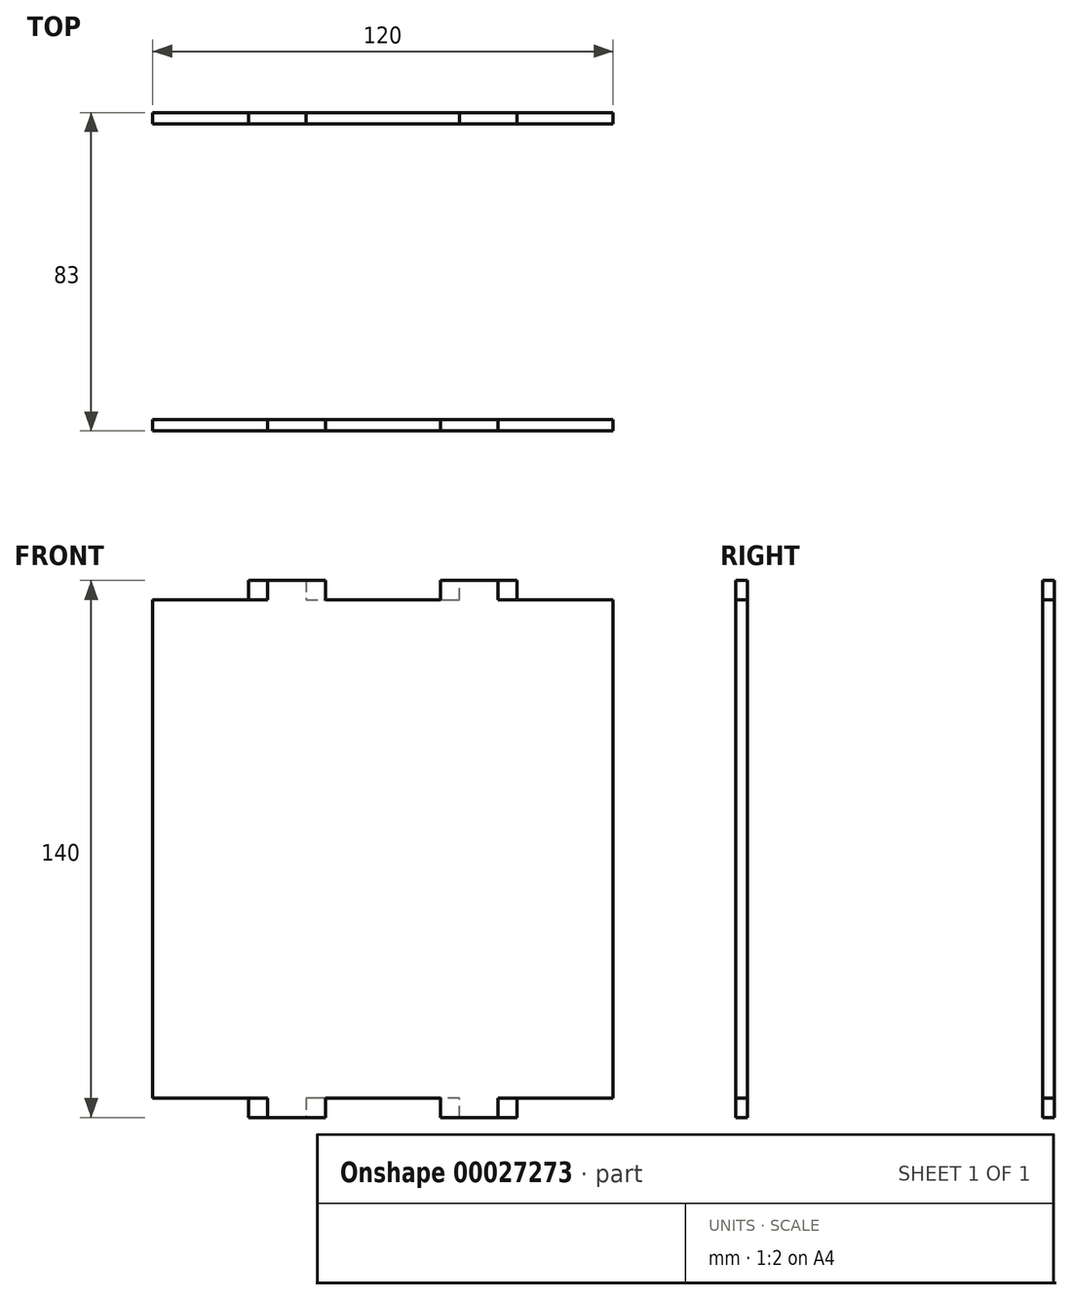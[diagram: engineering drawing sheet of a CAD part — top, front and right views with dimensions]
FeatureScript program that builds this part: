
annotation { "Feature Type Name" : "Feature", "Feature Type Description" : "" }
export const myFeature = defineFeature(function(context is Context, id is Id, definition is map)
    precondition{}
    {
        {
            var Q0;
            Q0=qCreatedBy(makeId("Front.planeOp"),FACE);
            var sketch = newSketch(context, id + "F0", { "sketchPlane" : qUnion([Q0])});
            skLineSegment(sketch, "E0", {"start": v(-60, 65) * mm, "end": v(-35, 65) * mm});
            skLineSegment(sketch, "E1", {"start": v(-35, 65) * mm, "end": v(-35, 70) * mm});
            skLineSegment(sketch, "E2", {"start": v(-35, 70) * mm, "end": v(-20, 70) * mm});
            skLineSegment(sketch, "E3", {"start": v(-20, 70) * mm, "end": v(-20, 65) * mm});
            skLineSegment(sketch, "E4", {"start": v(-20, 65) * mm, "end": v(20, 65) * mm});
            skLineSegment(sketch, "E5", {"start": v(20, 65) * mm, "end": v(20, 70) * mm});
            skLineSegment(sketch, "E6", {"start": v(20, 70) * mm, "end": v(35, 70) * mm});
            skLineSegment(sketch, "E7", {"start": v(35, 70) * mm, "end": v(35, 65) * mm});
            skLineSegment(sketch, "E8", {"start": v(35, 65) * mm, "end": v(60, 65) * mm});
            skLineSegment(sketch, "E9", {"start": v(60, 65) * mm, "end": v(60, -65) * mm});
            skLineSegment(sketch, "E10", {"start": v(60, -65) * mm, "end": v(35, -65) * mm});
            skLineSegment(sketch, "E11", {"start": v(35, -65) * mm, "end": v(35, -70) * mm});
            skLineSegment(sketch, "E12", {"start": v(35, -70) * mm, "end": v(20, -70) * mm});
            skLineSegment(sketch, "E13", {"start": v(20, -70) * mm, "end": v(20, -65) * mm});
            skLineSegment(sketch, "E14", {"start": v(20, -65) * mm, "end": v(-20, -65) * mm});
            skLineSegment(sketch, "E15", {"start": v(-20, -65) * mm, "end": v(-20, -70) * mm});
            skLineSegment(sketch, "E16", {"start": v(-20, -70) * mm, "end": v(-35, -70) * mm});
            skLineSegment(sketch, "E17", {"start": v(-35, -70) * mm, "end": v(-35, -65) * mm});
            skLineSegment(sketch, "E18", {"start": v(-35, -65) * mm, "end": v(-60, -65) * mm});
            skLineSegment(sketch, "E19", {"start": v(-60, -65) * mm, "end": v(-60, 65) * mm});
            skPoint(sketch, "E20", {"position": v(-60, 0) * mm});
            skLineSegment(sketch, "E21", {"start": v(-60, 0) * mm, "end": v(60, 0) * mm, "construction": true});
            skPoint(sketch, "E22", {"position": v(0, 0) * mm});
            skSolve(sketch);
        }
        {
            var Q0;
            Q0=makeQuery(id+"F0.imprint","IMPRINT",FACE,{"disambiguationData":[TD([[makeQuery(id+"F0.imprint","IMPRINT",EDGE,{"derivedFrom":sQuery(id+"F0.wireOp",EDGE,"E0")}),-1.0]])]});
            extrude(context, id + "F1", {"entities" : qUnion([Q0]), "depth" : 3 * mm});
        }
        {
            var Q0;
            Q0=qCreatedBy(makeId("Front.planeOp"),FACE);
            cPlane(context, id + "F2", {"entities" : qUnion([Q0]), "cplaneType" : CPlaneType.OFFSET, "offset" : 80 * mm, "width" : 150 * mm, "height" : 150 * mm});
        }
        {
            var Q0;
            Q0=qCreatedBy(id+"F2.planeOp",FACE);
            var sketch = newSketch(context, id + "F3", { "sketchPlane" : qUnion([Q0])});
            skLineSegment(sketch, "E23", {"start": v(-60, 65) * mm, "end": v(-30, 65) * mm});
            skLineSegment(sketch, "E24", {"start": v(-30, 65) * mm, "end": v(-30, 70) * mm});
            skLineSegment(sketch, "E25", {"start": v(-30, 70) * mm, "end": v(-15, 70) * mm});
            skLineSegment(sketch, "E26", {"start": v(-15, 70) * mm, "end": v(-15, 65) * mm});
            skLineSegment(sketch, "E27", {"start": v(-15, 65) * mm, "end": v(15, 65) * mm});
            skLineSegment(sketch, "E28", {"start": v(15, 65) * mm, "end": v(15, 70) * mm});
            skLineSegment(sketch, "E29", {"start": v(15, 70) * mm, "end": v(30, 70) * mm});
            skLineSegment(sketch, "E30", {"start": v(30, 70) * mm, "end": v(30, 65) * mm});
            skLineSegment(sketch, "E31", {"start": v(30, 65) * mm, "end": v(60, 65) * mm});
            skLineSegment(sketch, "E32", {"start": v(60, 65) * mm, "end": v(60, -65) * mm});
            skLineSegment(sketch, "E33", {"start": v(60, -65) * mm, "end": v(30, -65) * mm});
            skLineSegment(sketch, "E34", {"start": v(30, -65) * mm, "end": v(30, -70) * mm});
            skLineSegment(sketch, "E35", {"start": v(30, -70) * mm, "end": v(15, -70) * mm});
            skLineSegment(sketch, "E36", {"start": v(15, -70) * mm, "end": v(15, -65) * mm});
            skLineSegment(sketch, "E37", {"start": v(15, -65) * mm, "end": v(-15, -65) * mm});
            skLineSegment(sketch, "E38", {"start": v(-15, -65) * mm, "end": v(-15, -70) * mm});
            skLineSegment(sketch, "E39", {"start": v(-15, -70) * mm, "end": v(-30, -70) * mm});
            skLineSegment(sketch, "E40", {"start": v(-30, -70) * mm, "end": v(-30, -65) * mm});
            skLineSegment(sketch, "E41", {"start": v(-30, -65) * mm, "end": v(-60, -65) * mm});
            skLineSegment(sketch, "E42", {"start": v(-60, -65) * mm, "end": v(-60, 65) * mm});
            skPoint(sketch, "E43", {"position": v(-60, 0) * mm});
            skLineSegment(sketch, "E44", {"start": v(-60, 0) * mm, "end": v(60, 0) * mm, "construction": true});
            skPoint(sketch, "E45", {"position": v(0, 0) * mm});
            skSolve(sketch);
        }
        {
            var Q0;
            Q0=makeQuery(id+"F3.imprint","IMPRINT",FACE,{"disambiguationData":[TD([[makeQuery(id+"F3.imprint","IMPRINT",EDGE,{"derivedFrom":sQuery(id+"F3.wireOp",EDGE,"E23")}),-1.0]])]});
            extrude(context, id + "F4", {"entities" : qUnion([Q0]), "offsetDistance" : 25 * mm, "depth" : 3 * mm});
        }
    });
